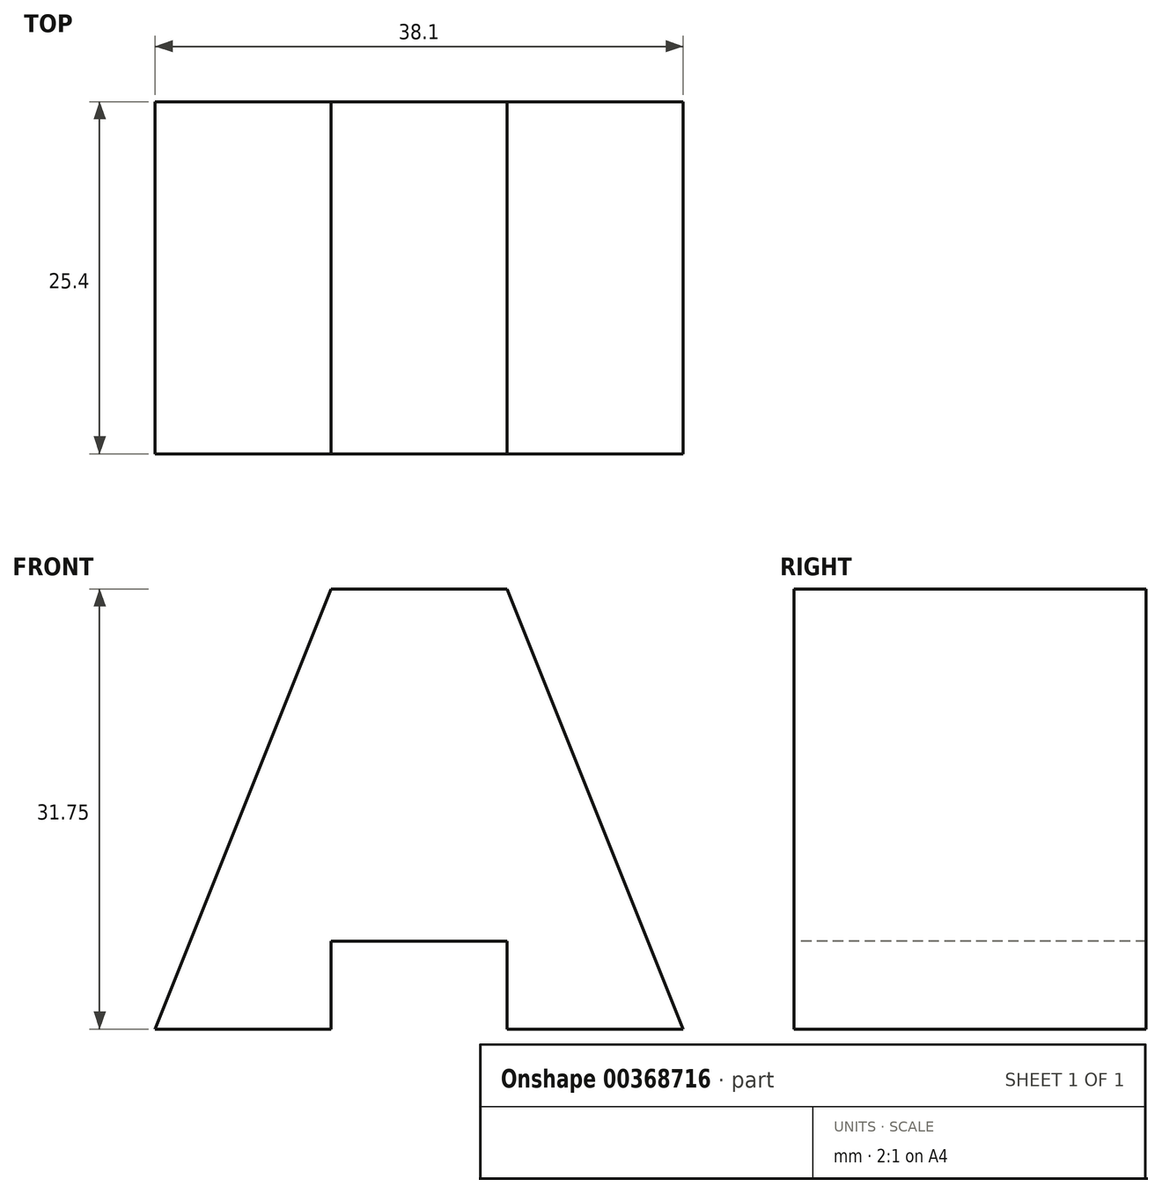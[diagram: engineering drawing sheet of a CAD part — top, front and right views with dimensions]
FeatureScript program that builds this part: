
annotation { "Feature Type Name" : "Feature", "Feature Type Description" : "" }
export const myFeature = defineFeature(function(context is Context, id is Id, definition is map)
    precondition{}
    {
        {
            var Q0;
            Q0=qCreatedBy(makeId("Front.planeOp"),FACE);
            var sketch = newSketch(context, id + "F0", { "sketchPlane" : qUnion([Q0])});
            skLineSegment(sketch, "E0", {"start": v(-37.47, 15.17) * mm, "end": v(0.63, 15.17) * mm});
            skLineSegment(sketch, "E1", {"start": v(0.63, 15.17) * mm, "end": v(-12.07, 46.92) * mm});
            skLineSegment(sketch, "E2", {"start": v(-12.07, 46.92) * mm, "end": v(-24.77, 46.92) * mm});
            skLineSegment(sketch, "E3", {"start": v(-24.77, 46.92) * mm, "end": v(-37.47, 15.17) * mm});
            skSolve(sketch);
        }
        {
            var Q0;
            Q0 = qSketchRegion(id + "F0", true);
            extrude(context, id + "F1", {"entities" : qUnion([Q0]), "depth" : 25.4 * mm});
        }
        {
            var Q0;
            Q0=makeQuery(id+"F1.opExtrude","CAP_FACE",FACE,{"disambiguationData":[OSD([sQuery(id+"F0.wireOp",EDGE,"E0"),sQuery(id+"F0.wireOp",EDGE,"E1"),sQuery(id+"F0.wireOp",EDGE,"E2"),sQuery(id+"F0.wireOp",EDGE,"E3")])],"isStart":false});
            var sketch = newSketch(context, id + "F2", { "sketchPlane" : qUnion([Q0])});
            skLineSegment(sketch, "E4", {"start": v(-24.77, 15.17) * mm, "end": v(-24.77, 21.52) * mm});
            skLineSegment(sketch, "E5", {"start": v(-24.77, 21.52) * mm, "end": v(-12.07, 21.52) * mm});
            skLineSegment(sketch, "E6", {"start": v(-12.07, 21.52) * mm, "end": v(-12.07, 15.17) * mm});
            skLineSegment(sketch, "E7", {"start": v(-12.07, 15.17) * mm, "end": v(-24.77, 15.17) * mm});
            skLineSegment(sketch, "E8", {"start": v(-12.07, 15.17) * mm, "end": v(0.63, 15.17) * mm});
            skLineSegment(sketch, "E9", {"start": v(-24.77, 15.17) * mm, "end": v(-37.47, 15.17) * mm});
            skSolve(sketch);
        }
        {
            var Q0;
            Q0=makeQuery(id+"F2.imprint","IMPRINT",FACE,{"disambiguationData":[TD([[makeQuery(id+"F2.imprint","IMPRINT",EDGE,{"derivedFrom":sQuery(id+"F2.wireOp",EDGE,"E4")}),-1.0]])]});
            extrude(context, id + "F3", {"entities" : qUnion([Q0]), "operationType" : NewBodyOperationType.REMOVE, "oppositeDirection" : true, "depth" : 25.4 * mm});
        }
    });
